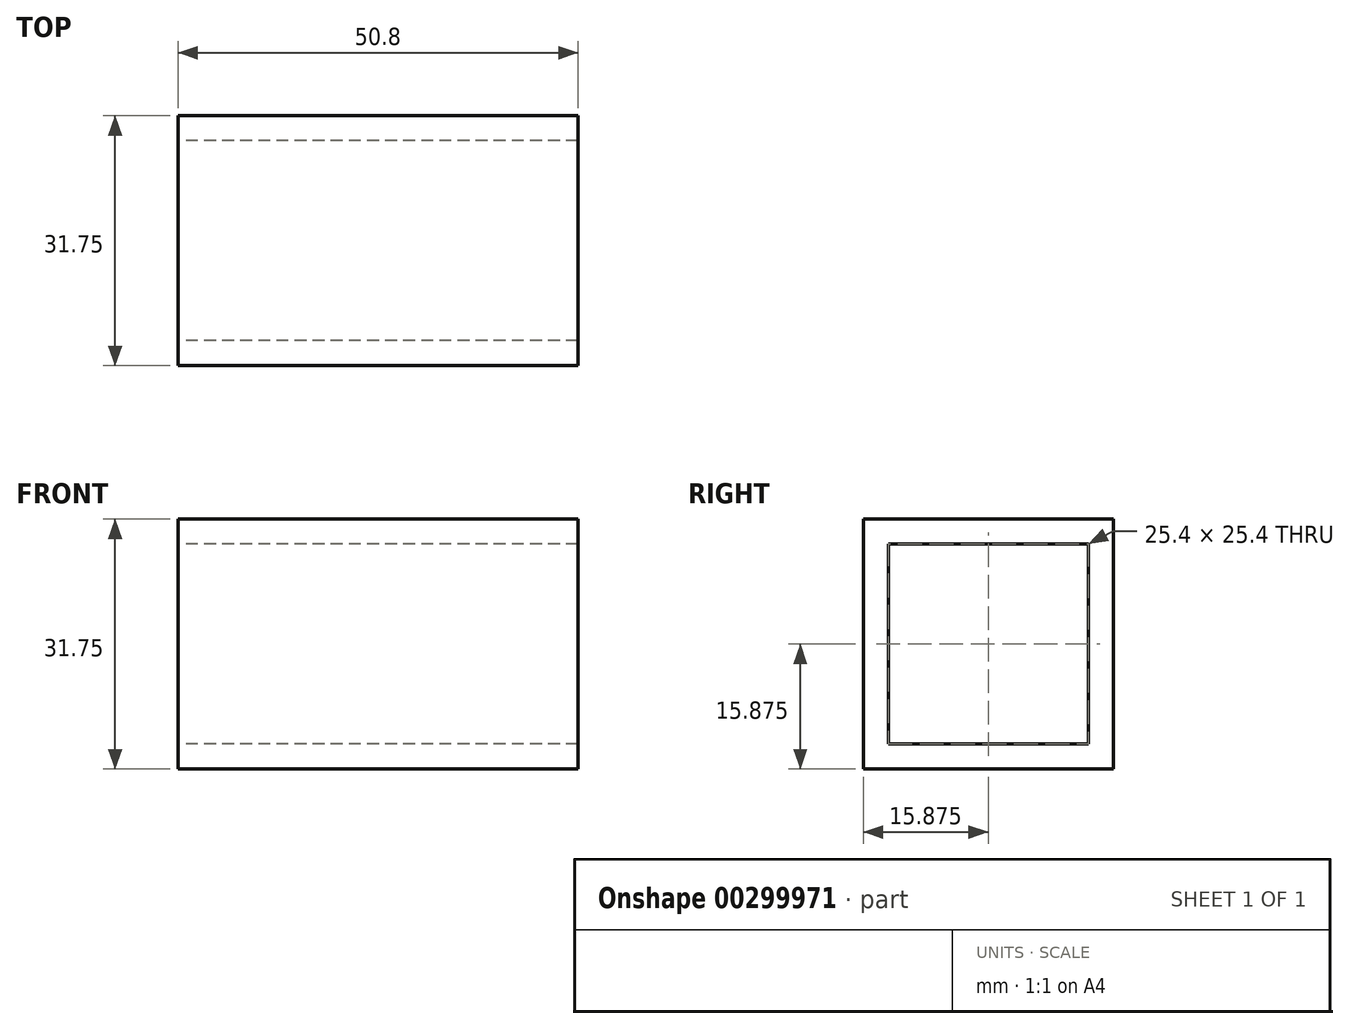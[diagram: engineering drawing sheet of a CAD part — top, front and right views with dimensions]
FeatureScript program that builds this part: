
annotation { "Feature Type Name" : "Feature", "Feature Type Description" : "" }
export const myFeature = defineFeature(function(context is Context, id is Id, definition is map)
    precondition{}
    {
        {
            var Q0;
            Q0=qCreatedBy(makeId("Right.planeOp"),FACE);
            var sketch = newSketch(context, id + "F0", { "sketchPlane" : qUnion([Q0])});
            skLineSegment(sketch, "E0.bottom", {"start": v(0, 0) * mm, "end": v(31.75, 0) * mm});
            skLineSegment(sketch, "E0.top", {"start": v(0, 31.75) * mm, "end": v(31.75, 31.75) * mm});
            skLineSegment(sketch, "E0.left", {"start": v(0, 0) * mm, "end": v(0, 31.75) * mm});
            skLineSegment(sketch, "E0.right", {"start": v(31.75, 0) * mm, "end": v(31.75, 31.75) * mm});
            skLineSegment(sketch, "E1.bottom", {"start": v(3.17, 28.57) * mm, "end": v(28.57, 28.57) * mm});
            skLineSegment(sketch, "E1.top", {"start": v(3.17, 3.17) * mm, "end": v(28.57, 3.17) * mm});
            skLineSegment(sketch, "E1.left", {"start": v(3.17, 28.57) * mm, "end": v(3.18, 3.17) * mm});
            skLineSegment(sketch, "E1.right", {"start": v(28.57, 28.57) * mm, "end": v(28.58, 3.17) * mm});
            skSolve(sketch);
        }
        {
            var Q0;
            Q0 = qSketchRegion(id + "F0", true);
            extrude(context, id + "F1", {"entities" : qUnion([Q0]), "depth" : 50.8 * mm, "offsetDistance" : 25 * mm});
        }
    });
